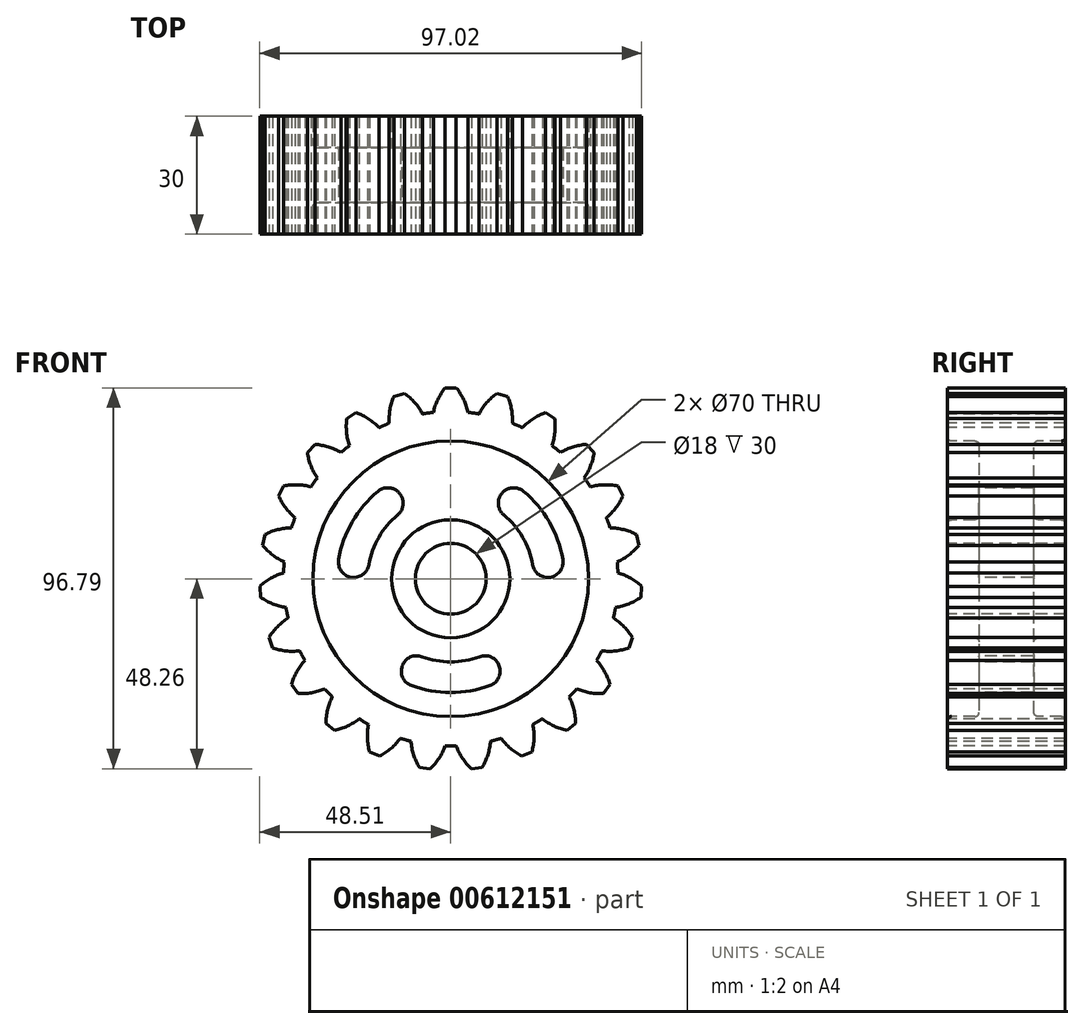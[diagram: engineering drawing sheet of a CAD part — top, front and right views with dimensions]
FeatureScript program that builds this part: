
annotation { "Feature Type Name" : "Feature", "Feature Type Description" : "" }
export const myFeature = defineFeature(function(context is Context, id is Id, definition is map)
    precondition{}
    {
        {
            var Q0;
            Q0=qCreatedBy(makeId("Right.planeOp"),FACE);
            var sketch = newSketch(context, id + "F0", { "sketchPlane" : qUnion([Q0])});
            skLineSegment(sketch, "E0", {"start": v(-15, 0) * mm, "end": v(15, 0) * mm});
            skLineSegment(sketch, "E1", {"start": v(15, 0) * mm, "end": v(15, 15) * mm});
            skLineSegment(sketch, "E2", {"start": v(15, 15) * mm, "end": v(7, 15) * mm});
            skLineSegment(sketch, "E3", {"start": v(7, 15) * mm, "end": v(7, 35) * mm});
            skLineSegment(sketch, "E4", {"start": v(7, 35) * mm, "end": v(15, 35) * mm});
            skLineSegment(sketch, "E5", {"start": v(15, 35) * mm, "end": v(15, 42.5) * mm});
            skLineSegment(sketch, "E6", {"start": v(15, 42.5) * mm, "end": v(-15, 42.5) * mm});
            skLineSegment(sketch, "E7", {"start": v(-15, 42.5) * mm, "end": v(-15, 35) * mm});
            skLineSegment(sketch, "E8", {"start": v(-15, 35) * mm, "end": v(-7, 35) * mm});
            skLineSegment(sketch, "E9", {"start": v(-7, 35) * mm, "end": v(-7, 15) * mm});
            skLineSegment(sketch, "E10", {"start": v(-7, 15) * mm, "end": v(-15, 15) * mm});
            skLineSegment(sketch, "E11", {"start": v(-15, 15) * mm, "end": v(-15, 0) * mm});
            skSolve(sketch);
        }
        {
            var Q0;
            Q0=makeQuery(id+"F0.imprint","IMPRINT",FACE,{"disambiguationData":[TD([[makeQuery(id+"F0.imprint","IMPRINT",EDGE,{"derivedFrom":sQuery(id+"F0.wireOp",EDGE,"E0")}),1.0]])]});
            var Q1;
            Q1=sQuery(id+"F0.wireOp",EDGE,"E0");
            revolve(context, id + "F1", {"entities" : qUnion([Q0]), "axis" : qUnion([Q1]), "revolveType" : RevolveType.FULL});
        }
        {
            var Q0;
            Q0=makeQuery(id+"F1.opRevolve","SWEPT_FACE",FACE,{"disambiguationData":[OSD([sQuery(id+"F0.wireOp",EDGE,"E11")])]});
            var sketch = newSketch(context, id + "F2", { "sketchPlane" : qUnion([Q0])});
            skCircle(sketch, "E12", {"center": v(0, 0) * mm, "radius": 9 * mm});
            skSolve(sketch);
        }
        {
            var Q0;
            Q0 = qSketchRegion(id + "F2", true);
            extrude(context, id + "F3", {"entities" : qUnion([Q0]), "operationType" : NewBodyOperationType.REMOVE, "endBound" : BoundingType.THROUGH_ALL, "oppositeDirection" : true, "depth" : 25 * mm, "offsetDistance" : 25 * mm});
        }
        {
            var Q0;
            Q0=makeQuery(id+"F1.opRevolve","SWEPT_FACE",FACE,{"disambiguationData":[OSD([sQuery(id+"F0.wireOp",EDGE,"E7")])]});
            var sketch = newSketch(context, id + "F4", { "sketchPlane" : qUnion([Q0])});
            skLineSegment(sketch, "E13", {"start": v(0, 0) * mm, "end": v(0, 48.53) * mm, "construction": true});
            skLineSegment(sketch, "E14", {"start": v(0, 48.53) * mm, "end": v(1.4, 48.53) * mm});
            skArc(sketch, "E15", {"start": v(4.4, 42.27) * mm, "mid": v(3.27, 45.57) * mm, "end": v(1.4, 48.53) * mm});
            skArc(sketch, "E16.MirrorCS", {"start": v(-4.4, 42.27) * mm, "mid": v(-3.27, 45.57) * mm, "end": v(-1.4, 48.53) * mm});
            skLineSegment(sketch, "E17.MirrorCS", {"start": v(0, 48.53) * mm, "end": v(-1.4, 48.53) * mm});
            skArc(sketch, "E18.1.0", {"start": v(-7.17, 41.9) * mm, "mid": v(-9.15, 44.77) * mm, "end": v(-11.74, 47.1) * mm});
            skLineSegment(sketch, "E18.1.1", {"start": v(-13.1, 46.73) * mm, "end": v(-11.74, 47.1) * mm});
            skLineSegment(sketch, "E18.1.2", {"start": v(-13.1, 46.73) * mm, "end": v(-14.44, 46.35) * mm});
            skArc(sketch, "E18.1.3", {"start": v(-15.64, 39.52) * mm, "mid": v(-15.44, 43) * mm, "end": v(-14.44, 46.35) * mm});
            skArc(sketch, "E18.2.0", {"start": v(-18.2, 38.4) * mm, "mid": v(-20.89, 40.64) * mm, "end": v(-24.02, 42.19) * mm});
            skLineSegment(sketch, "E18.2.1", {"start": v(-25.21, 41.46) * mm, "end": v(-24.02, 42.19) * mm});
            skLineSegment(sketch, "E18.2.2", {"start": v(-25.21, 41.46) * mm, "end": v(-26.4, 40.73) * mm});
            skArc(sketch, "E18.2.3", {"start": v(-25.72, 33.83) * mm, "mid": v(-26.47, 37.24) * mm, "end": v(-26.4, 40.73) * mm});
            skArc(sketch, "E18.3.0", {"start": v(-27.9, 32.07) * mm, "mid": v(-31.08, 33.5) * mm, "end": v(-34.5, 34.14) * mm});
            skLineSegment(sketch, "E18.3.1", {"start": v(-35.46, 33.12) * mm, "end": v(-34.5, 34.14) * mm});
            skLineSegment(sketch, "E18.3.2", {"start": v(-35.46, 33.12) * mm, "end": v(-36.42, 32.1) * mm});
            skArc(sketch, "E18.3.3", {"start": v(-33.9, 25.64) * mm, "mid": v(-35.54, 28.72) * mm, "end": v(-36.42, 32.1) * mm});
            skArc(sketch, "E18.4.0", {"start": v(-35.5, 23.35) * mm, "mid": v(-38.96, 23.87) * mm, "end": v(-42.44, 23.57) * mm});
            skLineSegment(sketch, "E18.4.1", {"start": v(-43.09, 22.33) * mm, "end": v(-42.44, 23.57) * mm});
            skLineSegment(sketch, "E18.4.2", {"start": v(-43.09, 22.33) * mm, "end": v(-43.73, 21.08) * mm});
            skArc(sketch, "E18.4.3", {"start": v(-39.56, 15.54) * mm, "mid": v(-41.97, 18.07) * mm, "end": v(-43.73, 21.08) * mm});
            skArc(sketch, "E18.5.0", {"start": v(-40.5, 12.9) * mm, "mid": v(-43.96, 12.47) * mm, "end": v(-47.23, 11.24) * mm});
            skLineSegment(sketch, "E18.5.1", {"start": v(-47.51, 9.87) * mm, "end": v(-47.23, 11.24) * mm});
            skLineSegment(sketch, "E18.5.2", {"start": v(-47.51, 9.87) * mm, "end": v(-47.8, 8.5) * mm});
            skArc(sketch, "E18.5.3", {"start": v(-42.28, 4.3) * mm, "mid": v(-45.29, 6.07) * mm, "end": v(-47.8, 8.5) * mm});
            skArc(sketch, "E18.6.0", {"start": v(-42.47, 1.5) * mm, "mid": v(-45.7, 0.15) * mm, "end": v(-48.5, -1.91) * mm});
            skLineSegment(sketch, "E18.6.1", {"start": v(-48.41, -3.31) * mm, "end": v(-48.5, -1.91) * mm});
            skLineSegment(sketch, "E18.6.2", {"start": v(-48.41, -3.31) * mm, "end": v(-48.32, -4.7) * mm});
            skArc(sketch, "E18.6.3", {"start": v(-41.87, -7.27) * mm, "mid": v(-45.25, -6.37) * mm, "end": v(-48.32, -4.7) * mm});
            skArc(sketch, "E18.7.0", {"start": v(-41.3, -10) * mm, "mid": v(-44.04, -12.18) * mm, "end": v(-46.2, -14.93) * mm});
            skLineSegment(sketch, "E18.7.1", {"start": v(-45.72, -16.25) * mm, "end": v(-46.2, -14.93) * mm});
            skLineSegment(sketch, "E18.7.2", {"start": v(-45.72, -16.25) * mm, "end": v(-45.26, -17.57) * mm});
            skArc(sketch, "E18.7.3", {"start": v(-38.36, -18.3) * mm, "mid": v(-41.85, -18.34) * mm, "end": v(-45.26, -17.57) * mm});
            skArc(sketch, "E18.8.0", {"start": v(-37.07, -20.78) * mm, "mid": v(-39.12, -23.61) * mm, "end": v(-40.45, -26.84) * mm});
            skLineSegment(sketch, "E18.8.1", {"start": v(-39.64, -27.98) * mm, "end": v(-40.45, -26.84) * mm});
            skLineSegment(sketch, "E18.8.2", {"start": v(-39.64, -27.98) * mm, "end": v(-38.84, -29.13) * mm});
            skArc(sketch, "E18.8.3", {"start": v(-32, -27.97) * mm, "mid": v(-35.35, -28.95) * mm, "end": v(-38.84, -29.13) * mm});
            skArc(sketch, "E18.9.0", {"start": v(-30.1, -30.01) * mm, "mid": v(-31.3, -33.3) * mm, "end": v(-31.71, -36.76) * mm});
            skLineSegment(sketch, "E18.9.1", {"start": v(-30.62, -37.64) * mm, "end": v(-31.71, -36.76) * mm});
            skLineSegment(sketch, "E18.9.2", {"start": v(-30.62, -37.64) * mm, "end": v(-29.54, -38.53) * mm});
            skArc(sketch, "E18.9.3", {"start": v(-23.26, -35.57) * mm, "mid": v(-26.23, -37.41) * mm, "end": v(-29.54, -38.53) * mm});
            skArc(sketch, "E18.10.0", {"start": v(-20.88, -37.02) * mm, "mid": v(-21.15, -40.5) * mm, "end": v(-20.62, -43.95) * mm});
            skLineSegment(sketch, "E18.10.1", {"start": v(-19.33, -44.5) * mm, "end": v(-20.62, -43.95) * mm});
            skLineSegment(sketch, "E18.10.2", {"start": v(-19.33, -44.5) * mm, "end": v(-18.05, -45.07) * mm});
            skArc(sketch, "E18.10.3", {"start": v(-12.8, -40.52) * mm, "mid": v(-15.16, -43.1) * mm, "end": v(-18.05, -45.07) * mm});
            skArc(sketch, "E18.11.0", {"start": v(-10.12, -41.28) * mm, "mid": v(-9.44, -44.7) * mm, "end": v(-8, -47.88) * mm});
            skLineSegment(sketch, "E18.11.1", {"start": v(-6.6, -48.07) * mm, "end": v(-8, -47.88) * mm});
            skLineSegment(sketch, "E18.11.2", {"start": v(-6.6, -48.07) * mm, "end": v(-5.22, -48.26) * mm});
            skArc(sketch, "E18.11.3", {"start": v(-1.4, -42.48) * mm, "mid": v(-2.97, -45.6) * mm, "end": v(-5.22, -48.26) * mm});
            skArc(sketch, "E18.12.0", {"start": v(1.4, -42.48) * mm, "mid": v(2.97, -45.6) * mm, "end": v(5.22, -48.26) * mm});
            skLineSegment(sketch, "E18.12.1", {"start": v(6.6, -48.07) * mm, "end": v(5.22, -48.26) * mm});
            skLineSegment(sketch, "E18.12.2", {"start": v(6.6, -48.07) * mm, "end": v(8, -47.88) * mm});
            skArc(sketch, "E18.12.3", {"start": v(10.12, -41.28) * mm, "mid": v(9.44, -44.7) * mm, "end": v(8, -47.88) * mm});
            skArc(sketch, "E18.13.0", {"start": v(12.8, -40.52) * mm, "mid": v(15.16, -43.1) * mm, "end": v(18.05, -45.07) * mm});
            skLineSegment(sketch, "E18.13.1", {"start": v(19.33, -44.5) * mm, "end": v(18.05, -45.07) * mm});
            skLineSegment(sketch, "E18.13.2", {"start": v(19.33, -44.5) * mm, "end": v(20.62, -43.95) * mm});
            skArc(sketch, "E18.13.3", {"start": v(20.88, -37.02) * mm, "mid": v(21.15, -40.5) * mm, "end": v(20.62, -43.95) * mm});
            skArc(sketch, "E18.14.0", {"start": v(23.26, -35.57) * mm, "mid": v(26.23, -37.41) * mm, "end": v(29.54, -38.53) * mm});
            skLineSegment(sketch, "E18.14.1", {"start": v(30.62, -37.64) * mm, "end": v(29.54, -38.53) * mm});
            skLineSegment(sketch, "E18.14.2", {"start": v(30.62, -37.64) * mm, "end": v(31.71, -36.76) * mm});
            skArc(sketch, "E18.14.3", {"start": v(30.1, -30.01) * mm, "mid": v(31.3, -33.3) * mm, "end": v(31.71, -36.76) * mm});
            skArc(sketch, "E18.15.0", {"start": v(32, -27.97) * mm, "mid": v(35.35, -28.95) * mm, "end": v(38.84, -29.13) * mm});
            skLineSegment(sketch, "E18.15.1", {"start": v(39.64, -27.98) * mm, "end": v(38.84, -29.13) * mm});
            skLineSegment(sketch, "E18.15.2", {"start": v(39.64, -27.98) * mm, "end": v(40.45, -26.84) * mm});
            skArc(sketch, "E18.15.3", {"start": v(37.07, -20.78) * mm, "mid": v(39.12, -23.61) * mm, "end": v(40.45, -26.84) * mm});
            skArc(sketch, "E18.16.0", {"start": v(38.36, -18.3) * mm, "mid": v(41.85, -18.34) * mm, "end": v(45.26, -17.57) * mm});
            skLineSegment(sketch, "E18.16.1", {"start": v(45.72, -16.25) * mm, "end": v(45.26, -17.57) * mm});
            skLineSegment(sketch, "E18.16.2", {"start": v(45.72, -16.25) * mm, "end": v(46.2, -14.93) * mm});
            skArc(sketch, "E18.16.3", {"start": v(41.3, -10) * mm, "mid": v(44.04, -12.18) * mm, "end": v(46.2, -14.93) * mm});
            skArc(sketch, "E18.17.0", {"start": v(41.87, -7.27) * mm, "mid": v(45.25, -6.37) * mm, "end": v(48.32, -4.7) * mm});
            skLineSegment(sketch, "E18.17.1", {"start": v(48.41, -3.31) * mm, "end": v(48.32, -4.7) * mm});
            skLineSegment(sketch, "E18.17.2", {"start": v(48.41, -3.31) * mm, "end": v(48.5, -1.91) * mm});
            skArc(sketch, "E18.17.3", {"start": v(42.47, 1.5) * mm, "mid": v(45.7, 0.15) * mm, "end": v(48.5, -1.91) * mm});
            skArc(sketch, "E18.18.0", {"start": v(42.28, 4.3) * mm, "mid": v(45.29, 6.07) * mm, "end": v(47.8, 8.5) * mm});
            skLineSegment(sketch, "E18.18.1", {"start": v(47.51, 9.87) * mm, "end": v(47.8, 8.5) * mm});
            skLineSegment(sketch, "E18.18.2", {"start": v(47.51, 9.87) * mm, "end": v(47.23, 11.24) * mm});
            skArc(sketch, "E18.18.3", {"start": v(40.5, 12.9) * mm, "mid": v(43.96, 12.47) * mm, "end": v(47.23, 11.24) * mm});
            skArc(sketch, "E18.19.0", {"start": v(39.56, 15.54) * mm, "mid": v(41.97, 18.07) * mm, "end": v(43.73, 21.08) * mm});
            skLineSegment(sketch, "E18.19.1", {"start": v(43.09, 22.33) * mm, "end": v(43.73, 21.08) * mm});
            skLineSegment(sketch, "E18.19.2", {"start": v(43.09, 22.33) * mm, "end": v(42.44, 23.57) * mm});
            skArc(sketch, "E18.19.3", {"start": v(35.5, 23.35) * mm, "mid": v(38.96, 23.87) * mm, "end": v(42.44, 23.57) * mm});
            skArc(sketch, "E18.20.0", {"start": v(33.9, 25.64) * mm, "mid": v(35.54, 28.72) * mm, "end": v(36.42, 32.1) * mm});
            skLineSegment(sketch, "E18.20.1", {"start": v(35.46, 33.12) * mm, "end": v(36.42, 32.1) * mm});
            skLineSegment(sketch, "E18.20.2", {"start": v(35.46, 33.12) * mm, "end": v(34.5, 34.14) * mm});
            skArc(sketch, "E18.20.3", {"start": v(27.9, 32.07) * mm, "mid": v(31.08, 33.5) * mm, "end": v(34.5, 34.14) * mm});
            skArc(sketch, "E18.21.0", {"start": v(25.72, 33.83) * mm, "mid": v(26.47, 37.24) * mm, "end": v(26.4, 40.73) * mm});
            skLineSegment(sketch, "E18.21.1", {"start": v(25.21, 41.46) * mm, "end": v(26.4, 40.73) * mm});
            skLineSegment(sketch, "E18.21.2", {"start": v(25.21, 41.46) * mm, "end": v(24.02, 42.19) * mm});
            skArc(sketch, "E18.21.3", {"start": v(18.2, 38.4) * mm, "mid": v(20.89, 40.64) * mm, "end": v(24.02, 42.19) * mm});
            skArc(sketch, "E18.22.0", {"start": v(15.64, 39.52) * mm, "mid": v(15.44, 43) * mm, "end": v(14.44, 46.35) * mm});
            skLineSegment(sketch, "E18.22.1", {"start": v(13.1, 46.73) * mm, "end": v(14.44, 46.35) * mm});
            skLineSegment(sketch, "E18.22.2", {"start": v(13.1, 46.73) * mm, "end": v(11.74, 47.1) * mm});
            skArc(sketch, "E18.22.3", {"start": v(7.17, 41.9) * mm, "mid": v(9.15, 44.77) * mm, "end": v(11.74, 47.1) * mm});
            skPoint(sketch, "E18.center", {"position": v(0, 0) * mm});
            skSolve(sketch);
        }
        {
            var Q0;
            Q0 = qSketchRegion(id + "F4", true);
            var Q1;
            {var subQ1=sQuery(id+"F4.wireOp",EDGE,"E18.20.0");Q1=makeQuery(id+"F4.imprint","IMPRINT",FACE,{"disambiguationData":[TD([[makeQuery(id+"F4.imprint","IMPRINT",EDGE,{"derivedFrom":subQ1}),1.0]])]});}
            var Q2;
            {var subQ1=sQuery(id+"F4.wireOp",EDGE,"E18.21.0");Q2=makeQuery(id+"F4.imprint","IMPRINT",FACE,{"disambiguationData":[TD([[makeQuery(id+"F4.imprint","IMPRINT",EDGE,{"derivedFrom":subQ1}),1.0]])]});}
            var Q3;
            {var subQ1=sQuery(id+"F4.wireOp",EDGE,"E18.22.0");Q3=makeQuery(id+"F4.imprint","IMPRINT",FACE,{"disambiguationData":[TD([[makeQuery(id+"F4.imprint","IMPRINT",EDGE,{"derivedFrom":subQ1}),1.0]])]});}
            var Q4;
            Q4=makeQuery(id+"F4.imprint","IMPRINT",FACE,{"disambiguationData":[TD([[makeQuery(id+"F4.imprint","IMPRINT",EDGE,{"derivedFrom":sQuery(id+"F4.wireOp",EDGE,"E14")}),-1.0]])]});
            var Q5;
            {var subQ1=sQuery(id+"F4.wireOp",EDGE,"E18.1.0");Q5=makeQuery(id+"F4.imprint","IMPRINT",FACE,{"disambiguationData":[TD([[makeQuery(id+"F4.imprint","IMPRINT",EDGE,{"derivedFrom":subQ1}),1.0]])]});}
            var Q6;
            {var subQ1=sQuery(id+"F4.wireOp",EDGE,"E18.2.0");Q6=makeQuery(id+"F4.imprint","IMPRINT",FACE,{"disambiguationData":[TD([[makeQuery(id+"F4.imprint","IMPRINT",EDGE,{"derivedFrom":subQ1}),1.0]])]});}
            var Q7;
            {var subQ1=sQuery(id+"F4.wireOp",EDGE,"E18.3.0");Q7=makeQuery(id+"F4.imprint","IMPRINT",FACE,{"disambiguationData":[TD([[makeQuery(id+"F4.imprint","IMPRINT",EDGE,{"derivedFrom":subQ1}),1.0]])]});}
            var Q8;
            {var subQ1=sQuery(id+"F4.wireOp",EDGE,"E18.4.0");Q8=makeQuery(id+"F4.imprint","IMPRINT",FACE,{"disambiguationData":[TD([[makeQuery(id+"F4.imprint","IMPRINT",EDGE,{"derivedFrom":subQ1}),1.0]])]});}
            var Q9;
            {var subQ1=sQuery(id+"F4.wireOp",EDGE,"E18.5.0");Q9=makeQuery(id+"F4.imprint","IMPRINT",FACE,{"disambiguationData":[TD([[makeQuery(id+"F4.imprint","IMPRINT",EDGE,{"derivedFrom":subQ1}),1.0]])]});}
            var Q10;
            {var subQ1=sQuery(id+"F4.wireOp",EDGE,"E18.6.0");Q10=makeQuery(id+"F4.imprint","IMPRINT",FACE,{"disambiguationData":[TD([[makeQuery(id+"F4.imprint","IMPRINT",EDGE,{"derivedFrom":subQ1}),1.0]])]});}
            var Q11;
            {var subQ1=sQuery(id+"F4.wireOp",EDGE,"E18.7.0");Q11=makeQuery(id+"F4.imprint","IMPRINT",FACE,{"disambiguationData":[TD([[makeQuery(id+"F4.imprint","IMPRINT",EDGE,{"derivedFrom":subQ1}),1.0]])]});}
            var Q12;
            {var subQ1=sQuery(id+"F4.wireOp",EDGE,"E18.8.0");Q12=makeQuery(id+"F4.imprint","IMPRINT",FACE,{"disambiguationData":[TD([[makeQuery(id+"F4.imprint","IMPRINT",EDGE,{"derivedFrom":subQ1}),1.0]])]});}
            var Q13;
            {var subQ1=sQuery(id+"F4.wireOp",EDGE,"E18.9.0");Q13=makeQuery(id+"F4.imprint","IMPRINT",FACE,{"disambiguationData":[TD([[makeQuery(id+"F4.imprint","IMPRINT",EDGE,{"derivedFrom":subQ1}),1.0]])]});}
            var Q14;
            {var subQ1=sQuery(id+"F4.wireOp",EDGE,"E18.10.0");Q14=makeQuery(id+"F4.imprint","IMPRINT",FACE,{"disambiguationData":[TD([[makeQuery(id+"F4.imprint","IMPRINT",EDGE,{"derivedFrom":subQ1}),1.0]])]});}
            var Q15;
            {var subQ1=sQuery(id+"F4.wireOp",EDGE,"E18.11.0");Q15=makeQuery(id+"F4.imprint","IMPRINT",FACE,{"disambiguationData":[TD([[makeQuery(id+"F4.imprint","IMPRINT",EDGE,{"derivedFrom":subQ1}),1.0]])]});}
            var Q16;
            {var subQ1=sQuery(id+"F4.wireOp",EDGE,"E18.12.0");Q16=makeQuery(id+"F4.imprint","IMPRINT",FACE,{"disambiguationData":[TD([[makeQuery(id+"F4.imprint","IMPRINT",EDGE,{"derivedFrom":subQ1}),1.0]])]});}
            var Q17;
            {var subQ1=sQuery(id+"F4.wireOp",EDGE,"E18.13.0");Q17=makeQuery(id+"F4.imprint","IMPRINT",FACE,{"disambiguationData":[TD([[makeQuery(id+"F4.imprint","IMPRINT",EDGE,{"derivedFrom":subQ1}),1.0]])]});}
            var Q18;
            {var subQ1=sQuery(id+"F4.wireOp",EDGE,"E18.14.0");Q18=makeQuery(id+"F4.imprint","IMPRINT",FACE,{"disambiguationData":[TD([[makeQuery(id+"F4.imprint","IMPRINT",EDGE,{"derivedFrom":subQ1}),1.0]])]});}
            var Q19;
            {var subQ1=sQuery(id+"F4.wireOp",EDGE,"E18.15.0");Q19=makeQuery(id+"F4.imprint","IMPRINT",FACE,{"disambiguationData":[TD([[makeQuery(id+"F4.imprint","IMPRINT",EDGE,{"derivedFrom":subQ1}),1.0]])]});}
            var Q20;
            {var subQ1=sQuery(id+"F4.wireOp",EDGE,"E18.16.0");Q20=makeQuery(id+"F4.imprint","IMPRINT",FACE,{"disambiguationData":[TD([[makeQuery(id+"F4.imprint","IMPRINT",EDGE,{"derivedFrom":subQ1}),1.0]])]});}
            var Q21;
            {var subQ1=sQuery(id+"F4.wireOp",EDGE,"E18.18.0");Q21=makeQuery(id+"F4.imprint","IMPRINT",FACE,{"disambiguationData":[TD([[makeQuery(id+"F4.imprint","IMPRINT",EDGE,{"derivedFrom":subQ1}),1.0]])]});}
            var Q22;
            {var subQ1=sQuery(id+"F4.wireOp",EDGE,"E18.17.0");Q22=makeQuery(id+"F4.imprint","IMPRINT",FACE,{"disambiguationData":[TD([[makeQuery(id+"F4.imprint","IMPRINT",EDGE,{"derivedFrom":subQ1}),1.0]])]});}
            var Q23;
            {var subQ1=sQuery(id+"F4.wireOp",EDGE,"E18.19.0");Q23=makeQuery(id+"F4.imprint","IMPRINT",FACE,{"disambiguationData":[TD([[makeQuery(id+"F4.imprint","IMPRINT",EDGE,{"derivedFrom":subQ1}),1.0]])]});}
            var Q24;
            Q24=makeQuery(id+"F1.opRevolve","SWEPT_FACE",FACE,{"disambiguationData":[OSD([sQuery(id+"F0.wireOp",EDGE,"E5")])]});
            extrude(context, id + "F5", {"entities" : qUnion([Q0, Q1, Q2, Q3, Q4, Q5, Q6, Q7, Q8, Q9, Q10, Q11, Q12, Q13, Q14, Q15, Q16, Q17, Q18, Q19, Q20, Q21, Q22, Q23]), "operationType" : NewBodyOperationType.ADD, "endBound" : BoundingType.UP_TO_SURFACE, "oppositeDirection" : true, "depth" : 25 * mm, "endBoundEntityFace" : qUnion([Q24]), "offsetDistance" : 25 * mm});
        }
        {
            var Q0;
            Q0=makeQuery(id+"F1.opRevolve","SWEPT_FACE",FACE,{"disambiguationData":[OSD([sQuery(id+"F0.wireOp",EDGE,"E9")])]});
            var sketch = newSketch(context, id + "F6", { "sketchPlane" : qUnion([Q0])});
            skArc(sketch, "E19", {"start": v(-10, -27.11) * mm, "mid": v(0, -28.9) * mm, "end": v(10, -27.11) * mm});
            skArc(sketch, "E20", {"start": v(-7.3, -19.8) * mm, "mid": v(0, -21.1) * mm, "end": v(7.3, -19.8) * mm});
            skLineSegment(sketch, "E21", {"start": v(0, 0) * mm, "end": v(10, -27.11) * mm, "construction": true});
            skLineSegment(sketch, "E22", {"start": v(0, 0) * mm, "end": v(-10, -27.11) * mm, "construction": true});
            skArc(sketch, "E23", {"start": v(-7.3, -19.8) * mm, "mid": v(-12.3, -22.1) * mm, "end": v(-10, -27.11) * mm});
            skArc(sketch, "E24", {"start": v(10, -27.11) * mm, "mid": v(12.3, -22.1) * mm, "end": v(7.3, -19.8) * mm});
            skArc(sketch, "E25.1.0", {"start": v(20.8, 3.58) * mm, "mid": v(18.27, 10.55) * mm, "end": v(13.5, 16.22) * mm});
            skArc(sketch, "E25.1.1", {"start": v(18.48, 22.22) * mm, "mid": v(12.99, 21.71) * mm, "end": v(13.5, 16.22) * mm});
            skArc(sketch, "E25.1.2", {"start": v(28.48, 4.9) * mm, "mid": v(25.03, 14.45) * mm, "end": v(18.48, 22.22) * mm});
            skArc(sketch, "E25.1.3", {"start": v(20.8, 3.58) * mm, "mid": v(25.3, 0.4) * mm, "end": v(28.48, 4.9) * mm});
            skArc(sketch, "E25.2.0", {"start": v(-13.5, 16.22) * mm, "mid": v(-18.27, 10.55) * mm, "end": v(-20.8, 3.58) * mm});
            skArc(sketch, "E25.2.1", {"start": v(-28.48, 4.9) * mm, "mid": v(-25.3, 0.4) * mm, "end": v(-20.8, 3.58) * mm});
            skArc(sketch, "E25.2.2", {"start": v(-18.48, 22.22) * mm, "mid": v(-25.03, 14.45) * mm, "end": v(-28.48, 4.9) * mm});
            skArc(sketch, "E25.2.3", {"start": v(-13.5, 16.22) * mm, "mid": v(-12.99, 21.71) * mm, "end": v(-18.48, 22.22) * mm});
            skSolve(sketch);
        }
        {
            var Q0;
            Q0=makeQuery(id+"F6.imprint","IMPRINT",FACE,{"disambiguationData":[TD([[makeQuery(id+"F6.imprint","IMPRINT",EDGE,{"derivedFrom":sQuery(id+"F6.wireOp",EDGE,"E25.2.0")}),-1.0]])]});
            var Q1;
            Q1=makeQuery(id+"F6.imprint","IMPRINT",FACE,{"disambiguationData":[TD([[makeQuery(id+"F6.imprint","IMPRINT",EDGE,{"derivedFrom":sQuery(id+"F6.wireOp",EDGE,"E25.1.0")}),-1.0]])]});
            var Q2;
            Q2=makeQuery(id+"F6.imprint","IMPRINT",FACE,{"disambiguationData":[TD([[makeQuery(id+"F6.imprint","IMPRINT",EDGE,{"derivedFrom":sQuery(id+"F6.wireOp",EDGE,"E19")}),1.0]])]});
            extrude(context, id + "F7", {"entities" : qUnion([Q0, Q1, Q2]), "operationType" : NewBodyOperationType.REMOVE, "endBound" : BoundingType.THROUGH_ALL, "oppositeDirection" : true, "depth" : 25 * mm, "offsetDistance" : 25 * mm});
        }
        {
            var Q0;
            Q0=makeQuery(id+"F1.opRevolve","SWEPT_EDGE",EDGE,{"disambiguationData":[OSD([sQuery(id+"F0.wireOp",EDGE,"E8"),sQuery(id+"F0.wireOp",EDGE,"E9")])]});
            var Q1;
            Q1=makeQuery(id+"F1.opRevolve","SWEPT_EDGE",EDGE,{"disambiguationData":[OSD([sQuery(id+"F0.wireOp",EDGE,"E7"),sQuery(id+"F0.wireOp",EDGE,"E8")])]});
            var Q2;
            Q2=makeQuery(id+"F1.opRevolve","SWEPT_EDGE",EDGE,{"disambiguationData":[OSD([sQuery(id+"F0.wireOp",EDGE,"E10"),sQuery(id+"F0.wireOp",EDGE,"E11")])]});
            var Q3;
            Q3=makeQuery(id+"F1.opRevolve","SWEPT_EDGE",EDGE,{"disambiguationData":[OSD([sQuery(id+"F0.wireOp",EDGE,"E4"),sQuery(id+"F0.wireOp",EDGE,"E5")])]});
            var Q4;
            Q4=makeQuery(id+"F1.opRevolve","SWEPT_EDGE",EDGE,{"disambiguationData":[OSD([sQuery(id+"F0.wireOp",EDGE,"E3"),sQuery(id+"F0.wireOp",EDGE,"E4")])]});
            var Q5;
            Q5=makeQuery(id+"F1.opRevolve","SWEPT_EDGE",EDGE,{"disambiguationData":[OSD([sQuery(id+"F0.wireOp",EDGE,"E1"),sQuery(id+"F0.wireOp",EDGE,"E2")])]});
            var Q6;
            Q6=makeQuery(id+"F1.opRevolve","SWEPT_EDGE",EDGE,{"disambiguationData":[OSD([sQuery(id+"F0.wireOp",EDGE,"E2"),sQuery(id+"F0.wireOp",EDGE,"E3")])]});
            var Q7;
            Q7=makeQuery(id+"F1.opRevolve","SWEPT_EDGE",EDGE,{"disambiguationData":[OSD([sQuery(id+"F0.wireOp",EDGE,"E9"),sQuery(id+"F0.wireOp",EDGE,"E10")])]});
            fillet(context, id + "F8", {"entities" : qUnion([Q0, Q1, Q2, Q3, Q4, Q5, Q6, Q7]), "radius" : 1 * mm, "tangentPropagation" : true, "allowEdgeOverflow" : false});
        }
        {
            var Q0;
            Q0=makeQuery(id+"F7.boolean.opBoolean","COPY",EDGE,{"derivedFrom":makeQuery(id+"F7.opExtrude","CAP_EDGE",EDGE,{"disambiguationData":[OSD([sQuery(id+"F6.wireOp",EDGE,"E20")])],"isStart":true})});
            var Q1;
            Q1=makeQuery(id+"F7.boolean.opBoolean","COPY",EDGE,{"derivedFrom":makeQuery(id+"F7.opExtrude","CAP_EDGE",EDGE,{"disambiguationData":[OSD([sQuery(id+"F6.wireOp",EDGE,"E25.1.0")])],"isStart":true})});
            var Q2;
            Q2=makeQuery(id+"F7.boolean.opBoolean","COPY",EDGE,{"derivedFrom":makeQuery(id+"F7.opExtrude","CAP_EDGE",EDGE,{"disambiguationData":[OSD([sQuery(id+"F6.wireOp",EDGE,"E25.2.0")])],"isStart":true})});
            var Q3;
            Q3=makeQuery(id+"F7.boolean.opBoolean","INTERSECT",EDGE,{"derivedFrom":[makeQuery(id+"F1.opRevolve","SWEPT_FACE",FACE,{"disambiguationData":[OSD([sQuery(id+"F0.wireOp",EDGE,"E3")])]}),makeQuery(id+"F7.opExtrude","SWEPT_FACE",FACE,{"disambiguationData":[OSD([sQuery(id+"F6.wireOp",EDGE,"E25.2.0")])]})]});
            var Q4;
            Q4=makeQuery(id+"F7.boolean.opBoolean","INTERSECT",EDGE,{"derivedFrom":[makeQuery(id+"F1.opRevolve","SWEPT_FACE",FACE,{"disambiguationData":[OSD([sQuery(id+"F0.wireOp",EDGE,"E3")])]}),makeQuery(id+"F7.opExtrude","SWEPT_FACE",FACE,{"disambiguationData":[OSD([sQuery(id+"F6.wireOp",EDGE,"E20")])]})]});
            var Q5;
            Q5=makeQuery(id+"F7.boolean.opBoolean","INTERSECT",EDGE,{"derivedFrom":[makeQuery(id+"F1.opRevolve","SWEPT_FACE",FACE,{"disambiguationData":[OSD([sQuery(id+"F0.wireOp",EDGE,"E3")])]}),makeQuery(id+"F7.opExtrude","SWEPT_FACE",FACE,{"disambiguationData":[OSD([sQuery(id+"F6.wireOp",EDGE,"E25.1.0")])]})]});
            fillet(context, id + "F9", {"entities" : qUnion([Q0, Q1, Q2, Q3, Q4, Q5]), "radius" : 0.3 * mm, "tangentPropagation" : true, "allowEdgeOverflow" : false});
        }
    });
